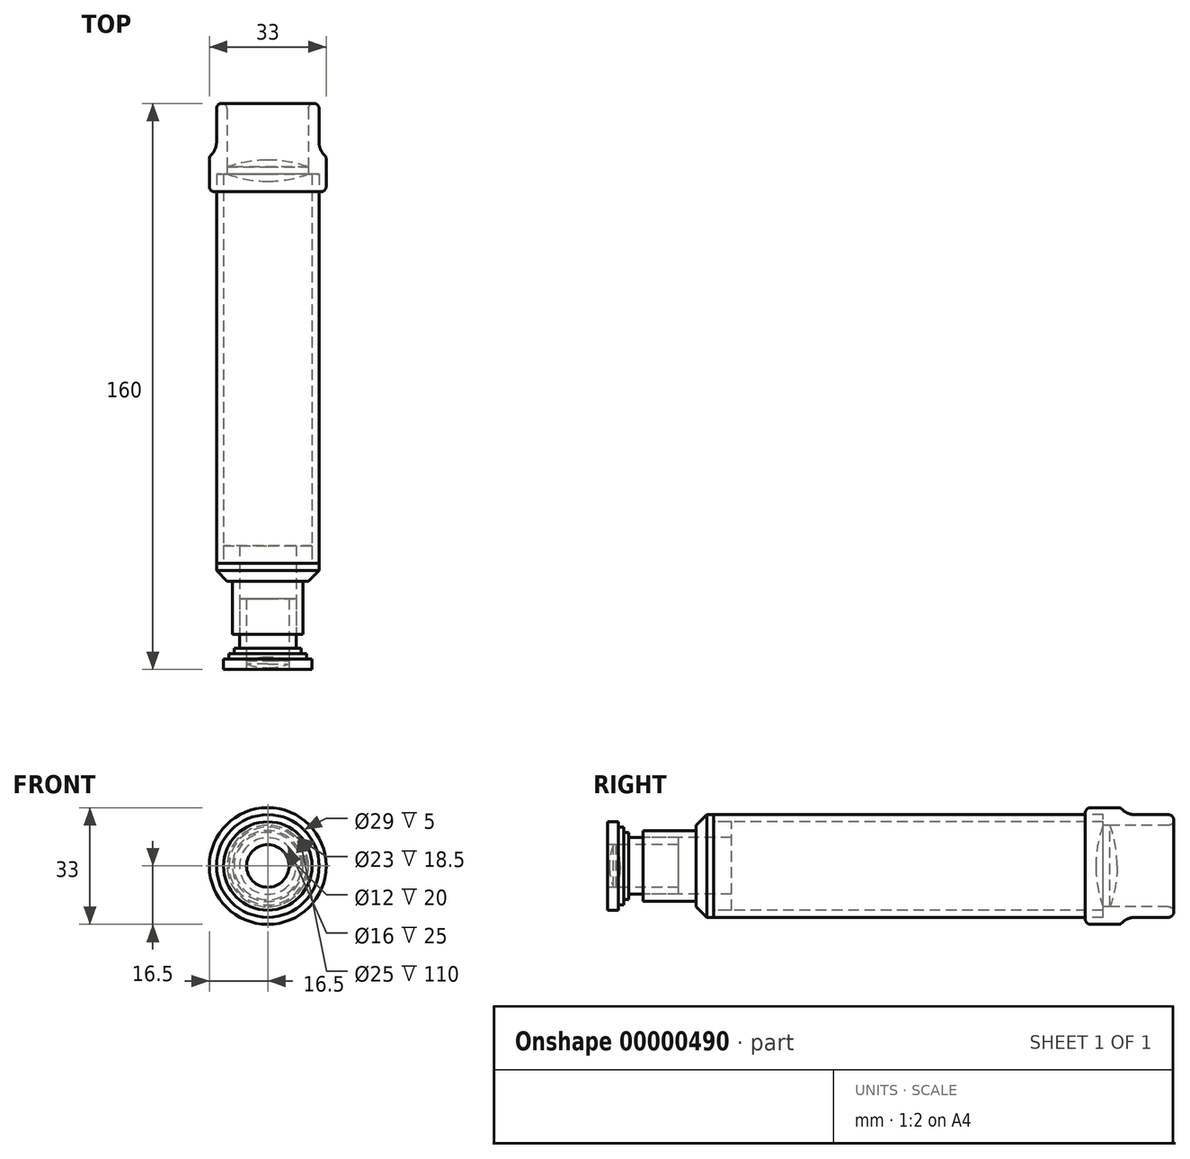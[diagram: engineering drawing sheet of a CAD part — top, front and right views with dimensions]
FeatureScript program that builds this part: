
annotation { "Feature Type Name" : "Feature", "Feature Type Description" : "" }
export const myFeature = defineFeature(function(context is Context, id is Id, definition is map)
    precondition{}
    {
        {
            var Q0;
            Q0    = qCreatedBy(makeId("Right.planeOp"), FACE);
            var sketch = newSketch(context, id + "F0", { "sketchPlane" : qUnion([Q0])});
            skLineSegment(sketch, "E0", {"start": v(-80, 0) * mm, "end": v(80, 0) * mm, "construction": true});
            skLineSegment(sketch, "E1", {"start": v(-50, 14.5) * mm, "end": v(60, 14.5) * mm, "construction": true});
            skLineSegment(sketch, "E2.bottom", {"start": v(-50, 14.5) * mm, "end": v(60, 14.5) * mm});
            skLineSegment(sketch, "E2.top", {"start": v(-50, 12.5) * mm, "end": v(60, 12.5) * mm});
            skLineSegment(sketch, "E2.left", {"start": v(-50, 14.5) * mm, "end": v(-50, 12.5) * mm});
            skLineSegment(sketch, "E2.right", {"start": v(60, 14.5) * mm, "end": v(60, 12.5) * mm});
            skLineSegment(sketch, "E3", {"start": v(55, 14.5) * mm, "end": v(55, 16.5) * mm});
            skLineSegment(sketch, "E4", {"start": v(55, 16.5) * mm, "end": v(65, 16.5) * mm});
            skLineSegment(sketch, "E5", {"start": v(65, 16.5) * mm, "end": v(65, 14.5) * mm});
            skLineSegment(sketch, "E6", {"start": v(65, 14.5) * mm, "end": v(80, 14.5) * mm});
            skLineSegment(sketch, "E7", {"start": v(80, 14.5) * mm, "end": v(80, 11.5) * mm});
            skLineSegment(sketch, "E8", {"start": v(80, 11.5) * mm, "end": v(60, 11.5) * mm});
            skLineSegment(sketch, "E9", {"start": v(60, 11.5) * mm, "end": v(60, 12.5) * mm});
            skLineSegment(sketch, "E10", {"start": v(-50, 14.5) * mm, "end": v(-55, 14.5) * mm});
            skLineSegment(sketch, "E11", {"start": v(-55, 14.5) * mm, "end": v(-55, 10) * mm});
            skLineSegment(sketch, "E12", {"start": v(-55, 10) * mm, "end": v(-70, 10) * mm});
            skLineSegment(sketch, "E13", {"start": v(-70, 10) * mm, "end": v(-70, 8) * mm});
            skLineSegment(sketch, "E14", {"start": v(-70, 8) * mm, "end": v(-45, 8) * mm});
            skLineSegment(sketch, "E15", {"start": v(-45, 8) * mm, "end": v(-45, 12.5) * mm});
            skArc(sketch, "E16", {"start": v(60, 11.5) * mm, "mid": v(58.5, 5.84) * mm, "end": v(58, 0) * mm});
            skArc(sketch, "E17", {"start": v(64, 0) * mm, "mid": v(63.5, 5.84) * mm, "end": v(62, 11.5) * mm});
            skLineSegment(sketch, "E18", {"start": v(58, 0) * mm, "end": v(64, 0) * mm});
            skLineSegment(sketch, "E19", {"start": v(-60, 8) * mm, "end": v(-60, 6) * mm});
            skLineSegment(sketch, "E20", {"start": v(-60, 6) * mm, "end": v(-80, 6) * mm});
            skLineSegment(sketch, "E21", {"start": v(-80, 6) * mm, "end": v(-80, 12.5) * mm});
            skLineSegment(sketch, "E22", {"start": v(-80, 12.5) * mm, "end": v(-77, 12.5) * mm});
            skLineSegment(sketch, "E23", {"start": v(-77, 12.5) * mm, "end": v(-77, 11) * mm});
            skLineSegment(sketch, "E24", {"start": v(-77, 11) * mm, "end": v(-75.5, 11) * mm});
            skLineSegment(sketch, "E25", {"start": v(-75.5, 11) * mm, "end": v(-75.5, 9.5) * mm});
            skLineSegment(sketch, "E26", {"start": v(-75.5, 9.5) * mm, "end": v(-74, 9.5) * mm});
            skLineSegment(sketch, "E27", {"start": v(-74, 9.5) * mm, "end": v(-74, 8) * mm});
            skLineSegment(sketch, "E28", {"start": v(-74, 8) * mm, "end": v(-70, 8) * mm});
            skArc(sketch, "E29", {"start": v(-78.43, 6) * mm, "mid": v(-79.23, 3.05) * mm, "end": v(-79.5, 0) * mm});
            skArc(sketch, "E30", {"start": v(-76.5, 0) * mm, "mid": v(-76.77, 3.05) * mm, "end": v(-77.57, 6) * mm});
            skLineSegment(sketch, "E31", {"start": v(-79.5, 0) * mm, "end": v(-76.5, 0) * mm});
            skPoint(sketch, "E32", {"position": v(-78, 0) * mm});
            skSolve(sketch);
        }
        {
            var Q0;
            {var subQ1=sQuery(id+"F0.wireOp",EDGE,"E2.left");Q0=makeQuery(id+"F0.imprint","IMPRINT",FACE,{"disambiguationData":[TD([[makeQuery(id+"F0.imprint","IMPRINT",EDGE,{"derivedFrom":subQ1}),1.0]])]});}
            var Q1;
            Q1=sQuery(id+"F0.wireOp",EDGE,"E0");
            revolve(context, id + "F1", {"entities" : qUnion([Q0]), "axis" : qUnion([Q1]), "revolveType" : RevolveType.FULL});
        }
        {
            var Q0;
            {var subQ5=sQuery(id+"F0.wireOp",EDGE,"E19");Q0=makeQuery(id+"F0.imprint","IMPRINT",FACE,{"disambiguationData":[TD([[makeQuery(id+"F0.imprint","IMPRINT",EDGE,{"derivedFrom":subQ5}),-1.0]])]});}
            var Q1;
            Q1=sQuery(id+"F0.wireOp",EDGE,"E0");
            revolve(context, id + "F2", {"entities" : qUnion([Q0]), "axis" : qUnion([Q1]), "revolveType" : RevolveType.FULL});
        }
        {
            var Q0;
            {var subQ4=sQuery(id+"F0.wireOp",EDGE,"E2.left");Q0=makeQuery(id+"F0.imprint","IMPRINT",FACE,{"disambiguationData":[TD([[makeQuery(id+"F0.imprint","IMPRINT",EDGE,{"derivedFrom":subQ4}),-1.0]])]});}
            var Q1;
            Q1=sQuery(id+"F0.wireOp",EDGE,"E0");
            revolve(context, id + "F3", {"entities" : qUnion([Q0]), "axis" : qUnion([Q1]), "revolveType" : RevolveType.FULL});
        }
        {
            var Q0;
            {var subQ5=sQuery(id+"F0.wireOp",EDGE,"E2.right");Q0=makeQuery(id+"F0.imprint","IMPRINT",FACE,{"disambiguationData":[TD([[makeQuery(id+"F0.imprint","IMPRINT",EDGE,{"derivedFrom":subQ5}),1.0]])]});}
            var Q1;
            Q1=sQuery(id+"F0.wireOp",EDGE,"E0");
            revolve(context, id + "F4", {"entities" : qUnion([Q0]), "axis" : qUnion([Q1]), "revolveType" : RevolveType.FULL});
        }
        {
            var Q0;
            {var subQ1=sQuery(id+"F0.wireOp",EDGE,"E16");Q0=makeQuery(id+"F0.imprint","IMPRINT",FACE,{"disambiguationData":[TD([[makeQuery(id+"F0.imprint","IMPRINT",EDGE,{"derivedFrom":subQ1}),1.0]])]});}
            var Q1;
            Q1=sQuery(id+"F0.wireOp",EDGE,"E0");
            revolve(context, id + "F5", {"entities" : qUnion([Q0]), "axis" : qUnion([Q1]), "revolveType" : RevolveType.FULL});
        }
        {
            var Q0;
            {var subQ1=sQuery(id+"F0.wireOp",EDGE,"E29");Q0=makeQuery(id+"F0.imprint","IMPRINT",FACE,{"disambiguationData":[TD([[makeQuery(id+"F0.imprint","IMPRINT",EDGE,{"derivedFrom":subQ1}),1.0]])]});}
            var Q1;
            Q1=sQuery(id+"F0.wireOp",EDGE,"E0");
            revolve(context, id + "F6", {"entities" : qUnion([Q0]), "axis" : qUnion([Q1]), "revolveType" : RevolveType.FULL});
        }
        {
            var Q0;
            Q0=makeQuery(id+"F3.opRevolve","SWEPT_EDGE",EDGE,{"disambiguationData":[OSD([sQuery(id+"F0.wireOp",EDGE,"E10"),sQuery(id+"F0.wireOp",EDGE,"E11")])]});
            chamfer(context, id + "F7", {"entities" : qUnion([Q0]), "width" : 3 * mm, "tangentPropagation" : true});
        }
        {
            var Q0;
            Q0=makeQuery(id+"F4.opRevolve","SWEPT_EDGE",EDGE,{"disambiguationData":[OSD([sQuery(id+"F0.wireOp",EDGE,"E5"),sQuery(id+"F0.wireOp",EDGE,"E6")])]});
            fillet(context, id + "F8", {"entities" : qUnion([Q0]), "radius" : 5 * mm, "tangentPropagation" : true, "allowEdgeOverflow" : false});
        }
        {
            var Q0;
            Q0=makeQuery(id+"F4.opRevolve","SWEPT_EDGE",EDGE,{"disambiguationData":[OSD([sQuery(id+"F0.wireOp",EDGE,"E6"),sQuery(id+"F0.wireOp",EDGE,"E7")])]});
            var Q1;
            Q1=makeQuery(id+"F4.opRevolve","SWEPT_EDGE",EDGE,{"disambiguationData":[OSD([sQuery(id+"F0.wireOp",EDGE,"E7"),sQuery(id+"F0.wireOp",EDGE,"E8")])]});
            var Q2;
            Q2=makeQuery(id+"F4.opRevolve","SWEPT_FACE",FACE,{"disambiguationData":[OSD([sQuery(id+"F0.wireOp",EDGE,"E4")])]});
            fillet(context, id + "F9", {"entities" : qUnion([Q0, Q1, Q2]), "radius" : 1.5 * mm, "tangentPropagation" : true, "allowEdgeOverflow" : false});
        }
    });
